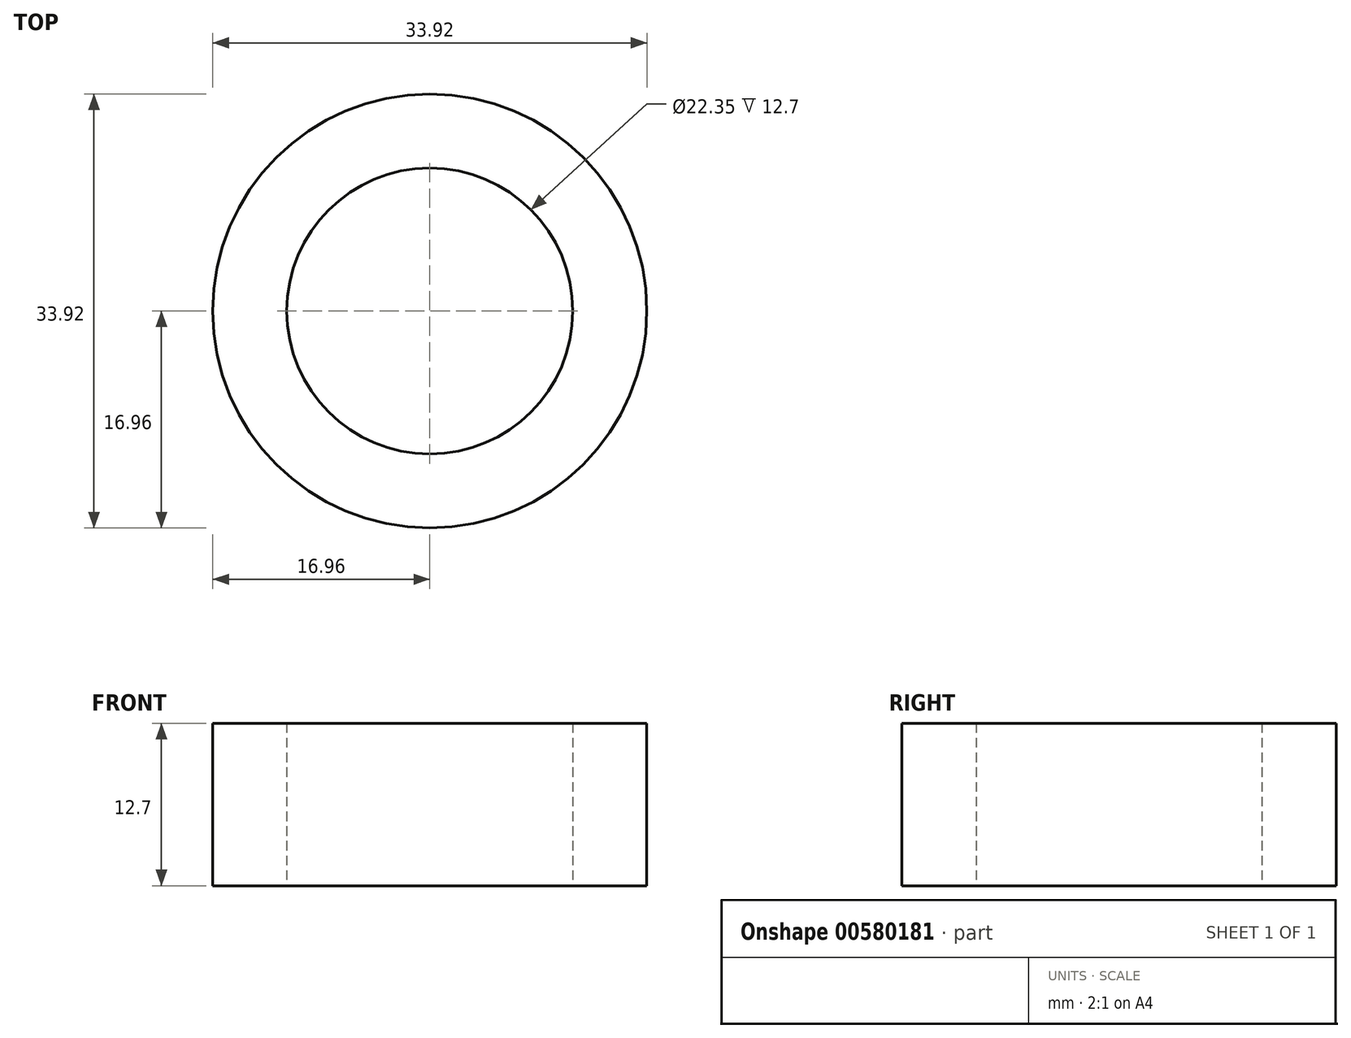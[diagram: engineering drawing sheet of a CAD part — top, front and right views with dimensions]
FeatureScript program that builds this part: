
annotation { "Feature Type Name" : "Feature", "Feature Type Description" : "" }
export const myFeature = defineFeature(function(context is Context, id is Id, definition is map)
    precondition{}
    {
        {
            var Q0;
            Q0=qCreatedBy(makeId("Top.planeOp"),FACE);
            var sketch = newSketch(context, id + "F0", { "sketchPlane" : qUnion([Q0])});
            skCircle(sketch, "E0", {"center": v(0, 0) * mm, "radius": 16.96 * mm});
            skSolve(sketch);
        }
        {
            var Q0;
            Q0=makeQuery(id+"F0.imprint","IMPRINT",FACE,{"disambiguationData":[TD([[makeQuery(id+"F0.imprint","IMPRINT",EDGE,{"derivedFrom":sQuery(id+"F0.wireOp",EDGE,"E0")}),1.0]])]});
            var Q1;
            Q1=sQuery(id+"F0.wireOp",EDGE,"E0");
            extrude(context, id + "F1", {"entities" : qUnion([Q0]), "surfaceEntities" : qUnion([Q1]), "depth" : 12.7 * mm, "offsetDistance" : 25.4 * mm});
        }
        {
            var Q0;
            Q0=qCreatedBy(makeId("Top.planeOp"),FACE);
            var sketch = newSketch(context, id + "F2", { "sketchPlane" : qUnion([Q0])});
            skCircle(sketch, "E1", {"center": v(0, 0) * mm, "radius": 11.17 * mm});
            skSolve(sketch);
        }
        {
            var Q0;
            Q0=qCreatedBy(makeId("Top.planeOp"),FACE);
            var sketch = newSketch(context, id + "F3", { "sketchPlane" : qUnion([Q0])});
            skCircle(sketch, "E2", {"center": v(-7.33, -8.54) * mm, "radius": 1.77 * mm});
            skPoint(sketch, "E2.first.point", {"position": v(-5.88, -9.56) * mm});
            skPoint(sketch, "E2.second.point", {"position": v(-8.53, -7.23) * mm});
            skPoint(sketch, "E2.third.point", {"position": v(-5.6, -8.12) * mm});
            skSolve(sketch);
        }
        {
            var Q0;
            Q0=makeQuery(id+"F3.imprint","IMPRINT",FACE,{"disambiguationData":[TD([[makeQuery(id+"F3.imprint","IMPRINT",EDGE,{"derivedFrom":sQuery(id+"F3.wireOp",EDGE,"E2")}),1.0]])]});
            extrude(context, id + "F4", {"entities" : qUnion([Q0]), "operationType" : NewBodyOperationType.ADD, "depth" : 12.7 * mm, "offsetDistance" : 25.4 * mm});
        }
        {
            var Q0;
            Q0=makeQuery(id+"F2.imprint","IMPRINT",FACE,{"disambiguationData":[TD([[makeQuery(id+"F2.imprint","IMPRINT",EDGE,{"derivedFrom":sQuery(id+"F2.wireOp",EDGE,"E1")}),1.0]])]});
            extrude(context, id + "F5", {"entities" : qUnion([Q0]), "operationType" : NewBodyOperationType.REMOVE, "oppositeDirection" : true, "depth" : -12.7 * mm, "offsetDistance" : 25.4 * mm});
        }
    });
